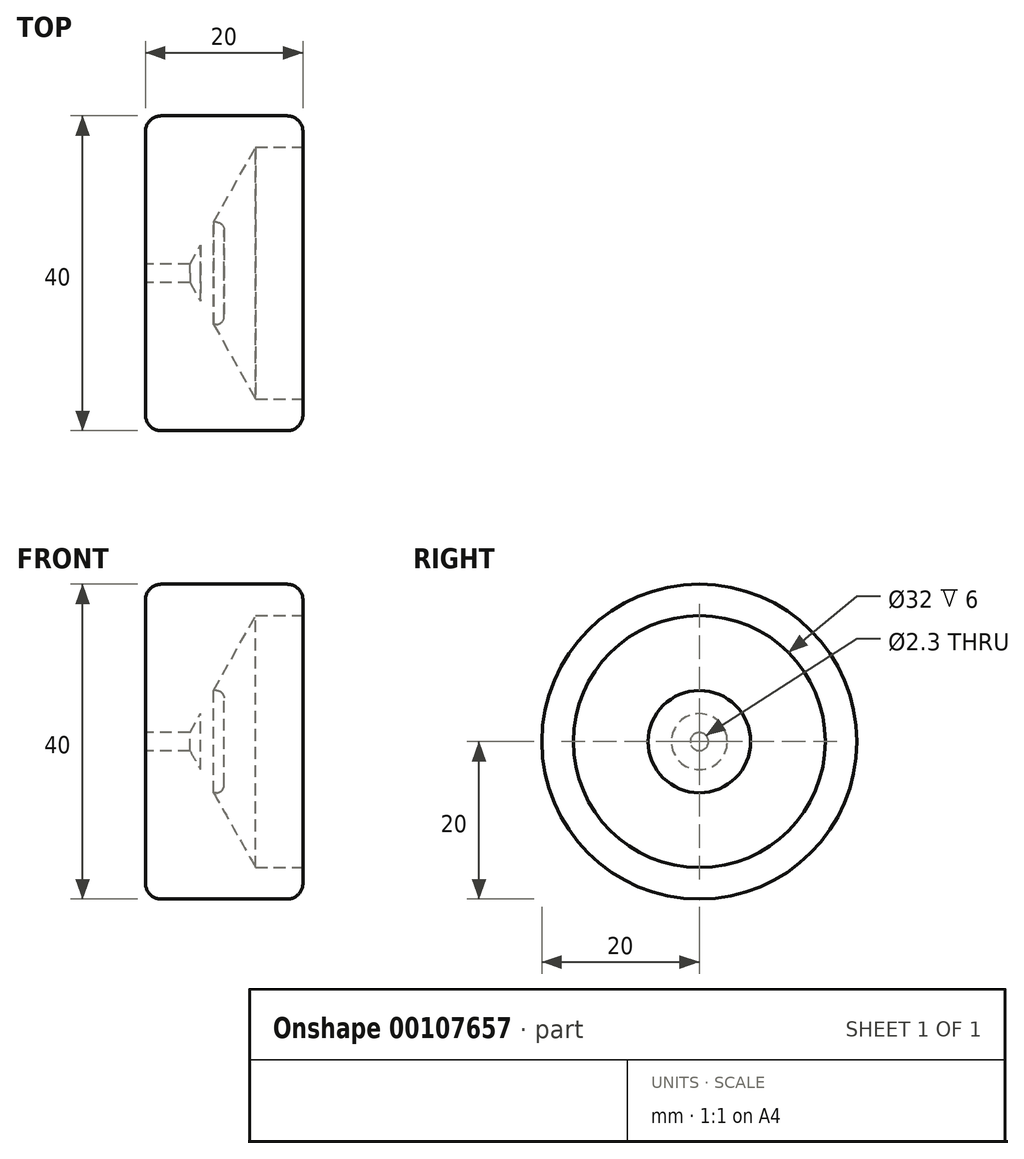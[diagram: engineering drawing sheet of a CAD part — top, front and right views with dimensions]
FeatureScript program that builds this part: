
annotation { "Feature Type Name" : "Feature", "Feature Type Description" : "" }
export const myFeature = defineFeature(function(context is Context, id is Id, definition is map)
    precondition{}
    {
        {
            var Q0;
            Q0=qCreatedBy(makeId("Top.planeOp"),FACE);
            var sketch = newSketch(context, id + "F0", { "sketchPlane" : qUnion([Q0])});
            skLineSegment(sketch, "E0", {"start": v(0, 0) * mm, "end": v(0, 20) * mm});
            skLineSegment(sketch, "E1", {"start": v(0, 20) * mm, "end": v(20, 20) * mm});
            skLineSegment(sketch, "E2", {"start": v(20, 20) * mm, "end": v(20, 16) * mm});
            skLineSegment(sketch, "E3", {"start": v(20, 16) * mm, "end": v(14, 16) * mm});
            skLineSegment(sketch, "E4", {"start": v(14, 16) * mm, "end": v(5, 0) * mm});
            skLineSegment(sketch, "E5", {"start": v(5, 0) * mm, "end": v(0, 0) * mm});
            skSolve(sketch);
        }
        {
            var Q0;
            Q0=makeQuery(id+"F0.imprint","IMPRINT",FACE,{"disambiguationData":[TD([[makeQuery(id+"F0.imprint","IMPRINT",EDGE,{"derivedFrom":sQuery(id+"F0.wireOp",EDGE,"E0")}),-1.0]])]});
            var Q1;
            Q1=sQuery(id+"F0.wireOp",EDGE,"E5");
            revolve(context, id + "F1", {"entities" : qUnion([Q0]), "axis" : qUnion([Q1]), "revolveType" : RevolveType.FULL});
        }
        {
            var Q0;
            Q0=makeQuery(id+"F1.opRevolve","SWEPT_FACE",FACE,{"disambiguationData":[OSD([sQuery(id+"F0.wireOp",EDGE,"E0")])]});
            var sketch = newSketch(context, id + "F2", { "sketchPlane" : qUnion([Q0])});
            skCircle(sketch, "E6", {"center": v(0, 0) * mm, "radius": 1.15 * mm});
            skSolve(sketch);
        }
        {
            var Q0;
            Q0=makeQuery(id+"F2.imprint","IMPRINT",FACE,{"disambiguationData":[TD([[makeQuery(id+"F2.imprint","IMPRINT",EDGE,{"derivedFrom":sQuery(id+"F2.wireOp",EDGE,"E6")}),1.0]])]});
            extrude(context, id + "F3", {"entities" : qUnion([Q0]), "operationType" : NewBodyOperationType.REMOVE, "oppositeDirection" : true, "depth" : 25 * mm});
        }
        {
            var Q0;
            Q0=makeQuery(id+"F1.opRevolve","SWEPT_EDGE",EDGE,{"disambiguationData":[OSD([sQuery(id+"F0.wireOp",EDGE,"E1"),sQuery(id+"F0.wireOp",EDGE,"E2")])]});
            var Q1;
            Q1=makeQuery(id+"F1.opRevolve","SWEPT_EDGE",EDGE,{"disambiguationData":[OSD([sQuery(id+"F0.wireOp",EDGE,"E0"),sQuery(id+"F0.wireOp",EDGE,"E1")])]});
            fillet(context, id + "F4", {"entities" : qUnion([Q0, Q1]), "radius" : 2 * mm, "tangentPropagation" : true, "allowEdgeOverflow" : false});
        }
        {
            var Q0;
            Q0=qCreatedBy(makeId("Right.planeOp"),FACE);
            cPlane(context, id + "F5", {"entities" : qUnion([Q0]), "cplaneType" : CPlaneType.OFFSET, "offset" : 3 * mm, "width" : 150 * mm, "height" : 150 * mm});
        }
        {
            var Q0;
            Q0=qCreatedBy(makeId("Right.planeOp"),FACE);
            cPlane(context, id + "F6", {"entities" : qUnion([Q0]), "cplaneType" : CPlaneType.OFFSET, "offset" : 7 * mm, "width" : 150 * mm, "height" : 150 * mm});
        }
        {
            var Q0;
            Q0=qCreatedBy(id+"F6.planeOp",FACE);
            var sketch = newSketch(context, id + "F7", { "sketchPlane" : qUnion([Q0])});
            skCircle(sketch, "E7.0", {"center": v(0, 0) * mm, "radius": 1.15 * mm});
            skCircle(sketch, "E8", {"center": v(0, 0) * mm, "radius": 6.5 * mm});
            skSolve(sketch);
        }
        {
            var Q0;
            Q0=makeQuery(id+"F7.imprint","IMPRINT",FACE,{"disambiguationData":[TD([[makeQuery(id+"F7.imprint","IMPRINT",EDGE,{"derivedFrom":sQuery(id+"F7.wireOp",EDGE,"E7.0")}),-1.0]])]});
            var Q1;
            Q1=makeQuery(id+"F7.imprint","IMPRINT",FACE,{"disambiguationData":[TD([[makeQuery(id+"F7.imprint","IMPRINT",EDGE,{"derivedFrom":sQuery(id+"F7.wireOp",EDGE,"E7.0")}),1.0]])]});
            extrude(context, id + "F8", {"entities" : qUnion([Q0, Q1]), "operationType" : NewBodyOperationType.ADD, "depth" : 3 * mm});
        }
        {
            var Q0;
            Q0=makeQuery(id+"F8.opExtrude","CAP_EDGE",EDGE,{"disambiguationData":[OSD([sQuery(id+"F7.wireOp",EDGE,"E8")])],"isStart":false});
            fillet(context, id + "F9", {"entities" : qUnion([Q0]), "radius" : 1 * mm, "tangentPropagation" : true, "allowEdgeOverflow" : false});
        }
    });
